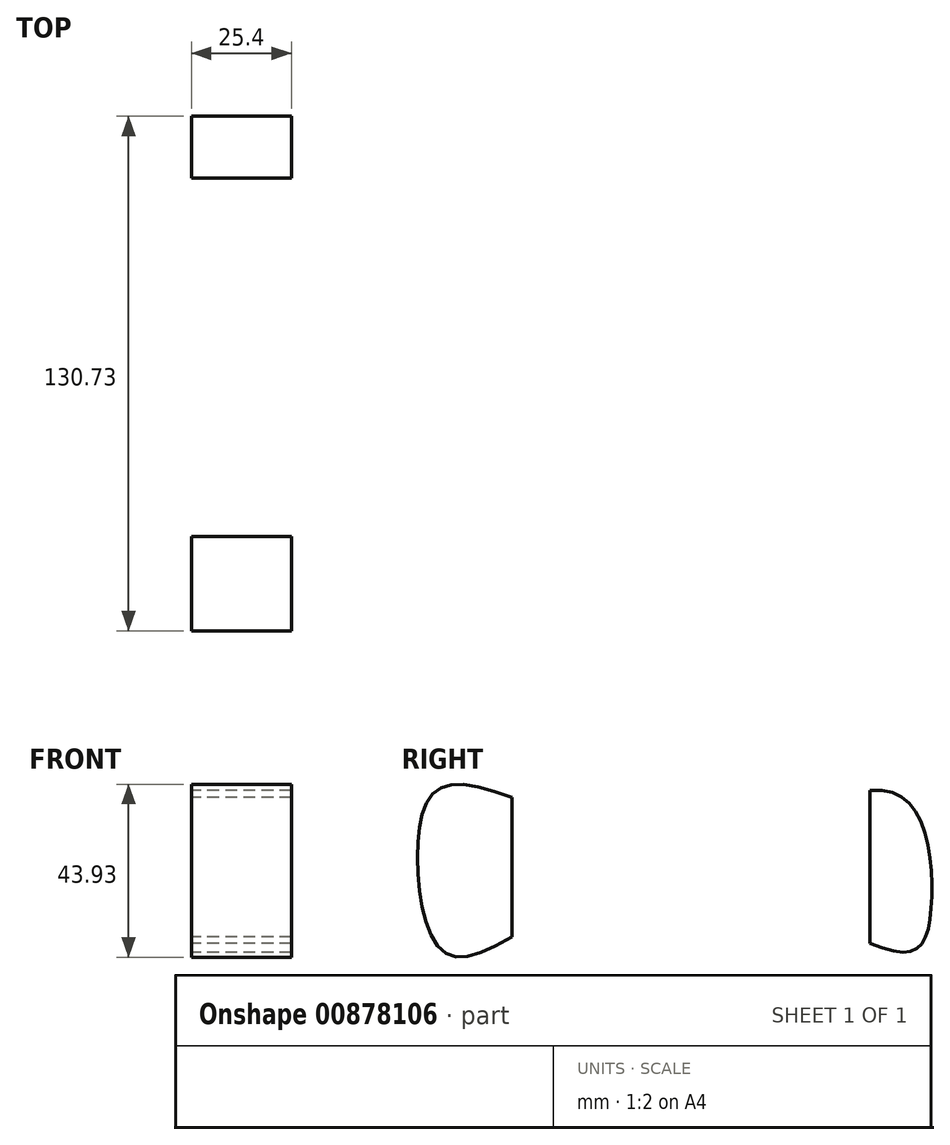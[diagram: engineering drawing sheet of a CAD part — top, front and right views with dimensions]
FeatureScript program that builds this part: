
annotation { "Feature Type Name" : "Feature", "Feature Type Description" : "" }
export const myFeature = defineFeature(function(context is Context, id is Id, definition is map)
    precondition{}
    {
        {
            var Q0;
            Q0=qCreatedBy(makeId("Right.planeOp"),FACE);
            var sketch = newSketch(context, id + "F0", { "sketchPlane" : qUnion([Q0])});
            skLineSegment(sketch, "E0.bottom", {"start": v(-35.9, 34.53) * mm, "end": v(42.39, 34.53) * mm});
            skLineSegment(sketch, "E0.top", {"start": v(-35.9, -49.72) * mm, "end": v(42.39, -49.72) * mm});
            skLineSegment(sketch, "E0.left", {"start": v(-42.25, 28.18) * mm, "end": v(-42.25, -43.37) * mm});
            skLineSegment(sketch, "E0.right", {"start": v(48.74, 28.18) * mm, "end": v(48.74, -43.37) * mm});
            skPoint(sketch, "E1.visualSharp", {"position": v(-42.25, 34.53) * mm});
            skArc(sketch, "E1.filletArc", {"start": v(-35.9, 34.53) * mm, "mid": v(-40.39, 32.67) * mm, "end": v(-42.25, 28.18) * mm});
            skPoint(sketch, "E2.visualSharp", {"position": v(-42.25, -49.72) * mm});
            skArc(sketch, "E2.filletArc", {"start": v(-42.25, -43.37) * mm, "mid": v(-40.39, -47.86) * mm, "end": v(-35.9, -49.72) * mm});
            skPoint(sketch, "E3.visualSharp", {"position": v(48.74, -49.72) * mm});
            skArc(sketch, "E3.filletArc", {"start": v(42.39, -49.72) * mm, "mid": v(46.88, -47.86) * mm, "end": v(48.74, -43.37) * mm});
            skPoint(sketch, "E4.visualSharp", {"position": v(48.74, 34.53) * mm});
            skArc(sketch, "E4.filletArc", {"start": v(48.74, 28.18) * mm, "mid": v(46.88, 32.67) * mm, "end": v(42.39, 34.53) * mm});
            skSolve(sketch);
        }
        {
            var Q0;
            Q0=makeQuery(id+"F0.imprint","IMPRINT",FACE,{"disambiguationData":[TD([[makeQuery(id+"F0.imprint","IMPRINT",EDGE,{"derivedFrom":sQuery(id+"F0.wireOp",EDGE,"E0.bottom")}),-1.0]])]});
            var sketch = newSketch(context, id + "F1", { "sketchPlane" : qUnion([Q0])});
            skFitSpline(sketch, "E5", {"points": [v(-56.82, -32.45) * mm, v(-4.4, -11.51) * mm, v(57.56, -31.35) * mm, v(64.3, -19.84) * mm, v(55.84, 8.7) * mm, v(-2.94, -1.71) * mm, v(-58.78, 11.02) * mm, v(-66.25, -8.08) * mm, v(-56.82, -32.45) * mm]});
            skSolve(sketch);
        }
        {
            var Q0;
            {var subQ0=sQuery(id+"F1.wireOp",EDGE,"E5");var subQ1=makeQuery(id+"F0.imprint","IMPRINT",EDGE,{"derivedFrom":sQuery(id+"F0.wireOp",EDGE,"E0.right")});var subQ2=makeQuery(id+"F1.imprint","INTERSECT",VERTEX,{"disambiguationData":[OD(0.0)],"derivedFrom":[subQ1,subQ0]});Q0=makeQuery(id+"F1.imprint","IMPRINT",FACE,{"disambiguationData":[TD([[makeQuery(id+"F1.imprint","IMPRINT",EDGE,{"disambiguationData":[TD([[subQ2,-1.0]])],"derivedFrom":subQ0}),1.0]])]});}
            var Q1;
            {var subQ0=sQuery(id+"F1.wireOp",EDGE,"E5");var subQ1=makeQuery(id+"F0.imprint","IMPRINT",EDGE,{"derivedFrom":sQuery(id+"F0.wireOp",EDGE,"E0.left")});var subQ2=makeQuery(id+"F1.imprint","INTERSECT",VERTEX,{"disambiguationData":[OD(0.0)],"derivedFrom":[subQ1,subQ0]});Q1=makeQuery(id+"F1.imprint","IMPRINT",FACE,{"disambiguationData":[TD([[makeQuery(id+"F1.imprint","IMPRINT",EDGE,{"disambiguationData":[TD([[subQ2,1.0]])],"derivedFrom":subQ0}),1.0]])]});}
            extrude(context, id + "F2", {"entities" : qUnion([Q0, Q1]), "depth" : 25.4 * mm, "offsetDistance" : 25.4 * mm});
        }
    });
